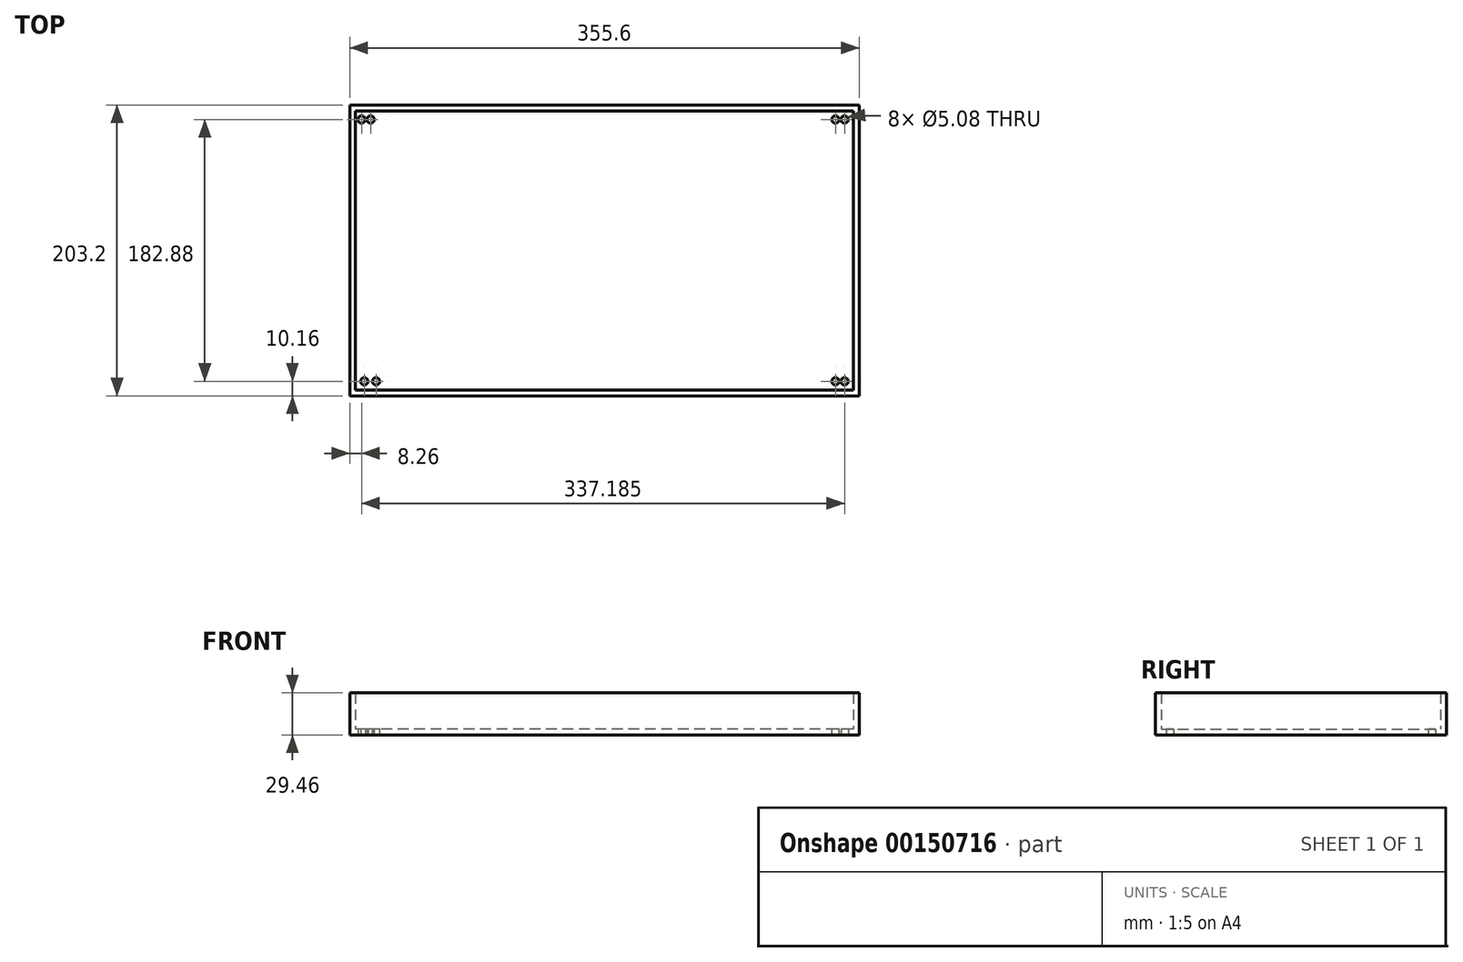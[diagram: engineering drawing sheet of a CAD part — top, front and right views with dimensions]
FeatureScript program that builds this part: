
annotation { "Feature Type Name" : "Feature", "Feature Type Description" : "" }
export const myFeature = defineFeature(function(context is Context, id is Id, definition is map)
    precondition{}
    {
        {
            var Q0;
            Q0=qCreatedBy(makeId("Top.planeOp"),FACE);
            var sketch = newSketch(context, id + "F0", { "sketchPlane" : qUnion([Q0])});
            skLineSegment(sketch, "E0.bottom", {"start": v(-174.48, 101.6) * mm, "end": v(181.12, 101.6) * mm});
            skLineSegment(sketch, "E0.top", {"start": v(-174.48, -101.6) * mm, "end": v(181.12, -101.6) * mm});
            skLineSegment(sketch, "E0.left", {"start": v(-174.48, 101.6) * mm, "end": v(-174.48, -101.6) * mm});
            skLineSegment(sketch, "E0.right", {"start": v(181.12, 101.6) * mm, "end": v(181.12, -101.6) * mm});
            skLineSegment(sketch, "E1", {"start": v(0, 101.6) * mm, "end": v(0, -101.6) * mm, "construction": true});
            skLineSegment(sketch, "E2.left", {"start": v(-174.48, 101.6) * mm, "end": v(-174.48, 88.9) * mm});
            skLineSegment(sketch, "E2.right", {"start": v(181.12, 101.6) * mm, "end": v(181.12, 88.9) * mm});
            skSolve(sketch);
        }
        {
            var Q0;
            Q0=makeQuery(id+"F0.imprint","IMPRINT",FACE,{"disambiguationData":[TD([[makeQuery(id+"F0.imprint","IMPRINT",EDGE,{"derivedFrom":sQuery(id+"F0.wireOp",EDGE,"E0.top")}),1.0]])]});
            extrude(context, id + "F1", {"entities" : qUnion([Q0]), "depth" : 4.06 * mm});
        }
        {
            var Q0;
            Q0=makeQuery(id+"F1.opExtrude","CAP_FACE",FACE,{"disambiguationData":[OSD([sQuery(id+"F0.wireOp",EDGE,"E0.bottom"),sQuery(id+"F0.wireOp",EDGE,"E0.top"),sQuery(id+"F0.wireOp",EDGE,"E0.left"),sQuery(id+"F0.wireOp",EDGE,"E0.right")])],"isStart":true});
            var sketch = newSketch(context, id + "F2", { "sketchPlane" : qUnion([Q0])});
            skCircle(sketch, "E3", {"center": v(170.96, 91.44) * mm, "radius": 1.9 * mm});
            skCircle(sketch, "E4", {"center": v(170.96, -91.44) * mm, "radius": 1.9 * mm});
            skCircle(sketch, "E5", {"center": v(-164.32, 91.44) * mm, "radius": 1.9 * mm});
            skCircle(sketch, "E6", {"center": v(-166.22, -91.44) * mm, "radius": 1.9 * mm});
            skPoint(sketch, "E7.orphan", {"position": v(181.12, 97.54) * mm});
            skPoint(sketch, "E8.orphan", {"position": v(177.06, 101.6) * mm});
            skPoint(sketch, "E9.orphan", {"position": v(-170.41, 101.6) * mm});
            skPoint(sketch, "E10.orphan", {"position": v(181.12, -97.54) * mm});
            skPoint(sketch, "E11.orphan", {"position": v(-174.48, -97.54) * mm});
            skSolve(sketch);
        }
        {
            var Q0;
            Q0=sQuery(id+"F2.wireOp",VERTEX,"E6.center");
            var Q1;
            Q1=sQuery(id+"F2.wireOp",VERTEX,"E4.center");
            var Q2;
            Q2=sQuery(id+"F2.wireOp",VERTEX,"E5.center");
            var Q3;
            Q3=sQuery(id+"F2.wireOp",VERTEX,"E3.center");
            var Q4;
            Q4=makeQuery(id+"F1.opExtrude","SWEPT_BODY",BODY,{"disambiguationData":[OSD([sQuery(id+"F0.wireOp",EDGE,"E0.top"),sQuery(id+"F0.wireOp",EDGE,"E0.left"),sQuery(id+"F0.wireOp",EDGE,"E0.right"),sQuery(id+"F0.wireOp",EDGE,"E0.bottom"),sQuery(id+"F0.wireOp",EDGE,"E2.left"),sQuery(id+"F0.wireOp",EDGE,"E2.right")])]});
            hole(context, id + "F3", {"style" : HoleStyle.SIMPLE, "endStyle" : HoleEndStyle.THROUGH, "holeDiameter" : 5.08 * mm, "locations" : qUnion([Q0, Q1, Q2, Q3]), "scope" : qUnion([Q4]), "isTappedThrough" : true});
        }
        {
            var Q0;
            Q0=makeQuery(id+"F1.opExtrude","CAP_FACE",FACE,{"disambiguationData":[OSD([sQuery(id+"F0.wireOp",EDGE,"E0.top"),sQuery(id+"F0.wireOp",EDGE,"E0.left"),sQuery(id+"F0.wireOp",EDGE,"E0.right"),sQuery(id+"F0.wireOp",EDGE,"E0.bottom"),sQuery(id+"F0.wireOp",EDGE,"E2.left"),sQuery(id+"F0.wireOp",EDGE,"E2.right")])],"isStart":false});
            var sketch = newSketch(context, id + "F4", { "sketchPlane" : qUnion([Q0])});
            skLineSegment(sketch, "E12", {"start": v(177.06, -97.54) * mm, "end": v(177.06, 97.54) * mm});
            skLineSegment(sketch, "E13", {"start": v(177.06, 101.6) * mm, "end": v(181.12, 101.6) * mm});
            skLineSegment(sketch, "E14", {"start": v(-170.41, 97.54) * mm, "end": v(-170.41, -97.54) * mm});
            skLineSegment(sketch, "E15", {"start": v(177.06, -97.54) * mm, "end": v(-170.41, -97.54) * mm});
            skLineSegment(sketch, "E16", {"start": v(177.06, 97.54) * mm, "end": v(-170.41, 97.54) * mm});
            skPoint(sketch, "E17.orphan", {"position": v(181.12, 97.54) * mm});
            skPoint(sketch, "E18.orphan", {"position": v(-174.48, 97.54) * mm});
            skPoint(sketch, "E19.orphan", {"position": v(-174.48, -97.54) * mm});
            skPoint(sketch, "E20.orphan", {"position": v(-170.41, -101.6) * mm});
            skSolve(sketch);
        }
        {
            var Q0;
            Q0=makeQuery(id+"F4.imprint","IMPRINT",FACE,{"disambiguationData":[TD([[makeQuery(id+"F4.imprint","IMPRINT",EDGE,{"derivedFrom":sQuery(id+"F4.wireOp",EDGE,"E12")}),-1.0]])]});
            extrude(context, id + "F5", {"entities" : qUnion([Q0]), "operationType" : NewBodyOperationType.ADD, "depth" : 25.4 * mm});
        }
        {
            var Q0;
            Q0=makeQuery(id+"F4.imprint","IMPRINT",FACE,{"disambiguationData":[TD([[makeQuery(id+"F4.imprint","IMPRINT",EDGE,{"derivedFrom":sQuery(id+"F4.wireOp",EDGE,"E12")}),1.0]])]});
            var sketch = newSketch(context, id + "F6", { "sketchPlane" : qUnion([Q0])});
            skCircle(sketch, "E21", {"center": v(-156.06, -91.44) * mm, "radius": 1.9 * mm});
            skCircle(sketch, "E22", {"center": v(-159.87, 91.44) * mm, "radius": 1.9 * mm});
            skCircle(sketch, "E23", {"center": v(164.61, 91.44) * mm, "radius": 1.9 * mm});
            skCircle(sketch, "E24", {"center": v(164.61, -91.44) * mm, "radius": 1.9 * mm});
            skSolve(sketch);
        }
        {
            var Q0;
            Q0=sQuery(id+"F6.wireOp",VERTEX,"E21.center");
            var Q1;
            Q1=sQuery(id+"F6.wireOp",VERTEX,"E24.center");
            var Q2;
            Q2=sQuery(id+"F6.wireOp",VERTEX,"E23.center");
            var Q3;
            Q3=sQuery(id+"F6.wireOp",VERTEX,"E22.center");
            var Q4;
            Q4=makeQuery(id+"F1.opExtrude","SWEPT_BODY",BODY,{"disambiguationData":[OSD([sQuery(id+"F0.wireOp",EDGE,"E0.top"),sQuery(id+"F0.wireOp",EDGE,"E0.left"),sQuery(id+"F0.wireOp",EDGE,"E0.right"),sQuery(id+"F0.wireOp",EDGE,"E0.bottom"),sQuery(id+"F0.wireOp",EDGE,"E2.left"),sQuery(id+"F0.wireOp",EDGE,"E2.right")])]});
            hole(context, id + "F7", {"style" : HoleStyle.SIMPLE, "endStyle" : HoleEndStyle.THROUGH, "holeDiameter" : 5.08 * mm, "locations" : qUnion([Q0, Q1, Q2, Q3]), "scope" : qUnion([Q4]), "isTappedThrough" : true});
        }
    });
